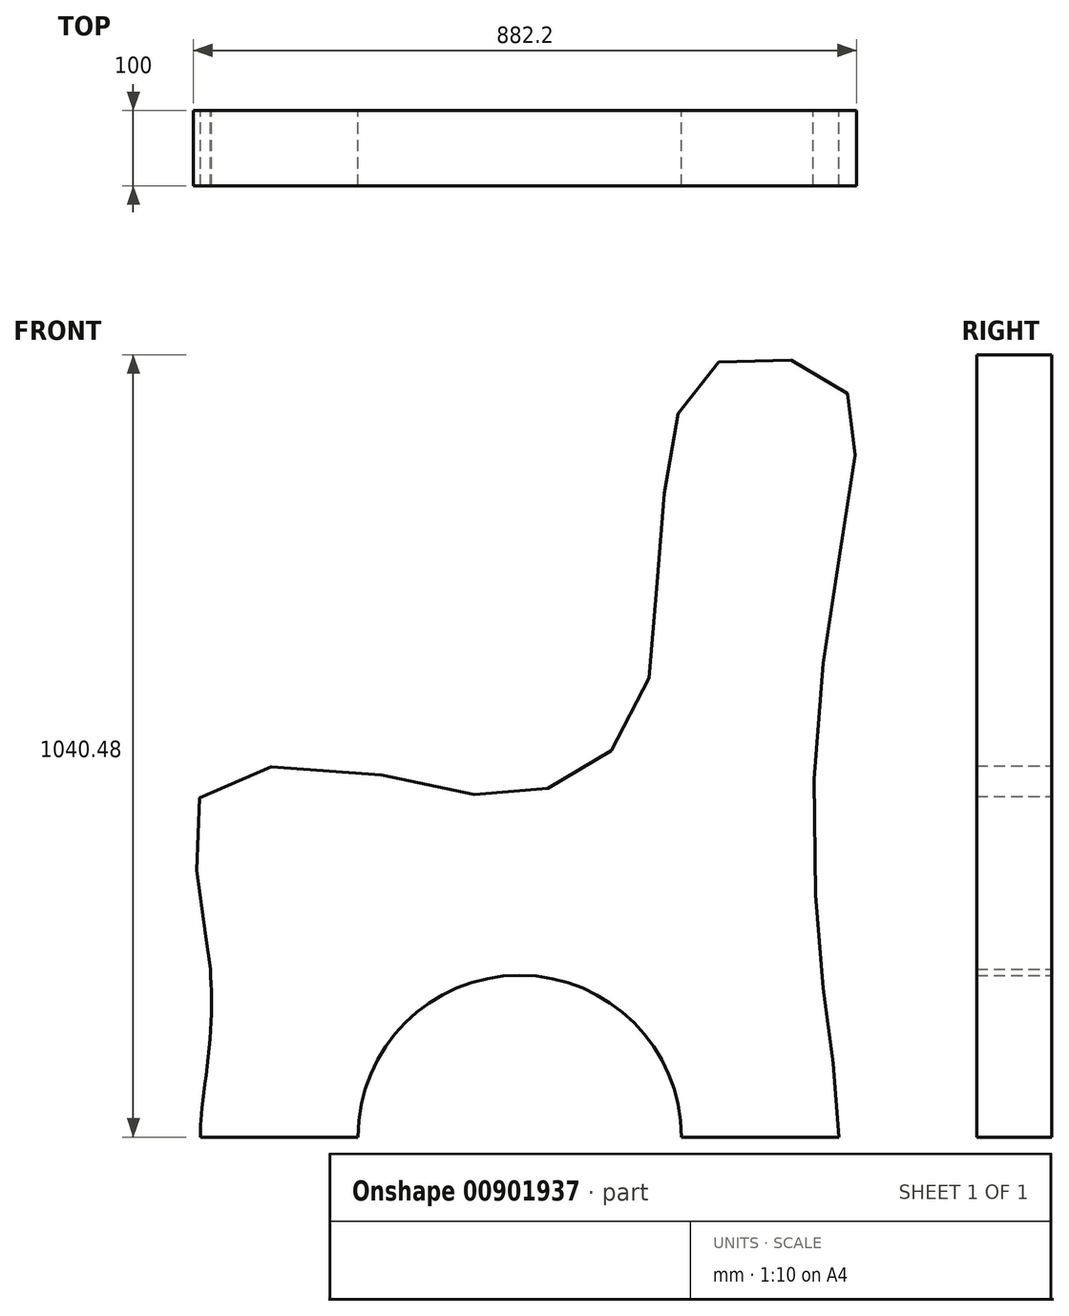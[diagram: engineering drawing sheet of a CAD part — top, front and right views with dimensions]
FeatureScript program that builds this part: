
annotation { "Feature Type Name" : "Feature", "Feature Type Description" : "" }
export const myFeature = defineFeature(function(context is Context, id is Id, definition is map)
    precondition{}
    {
        {
            var Q0;
            Q0=qCreatedBy(makeId("Front.planeOp"),FACE);
            var sketch = newSketch(context, id + "F0", { "sketchPlane" : qUnion([Q0])});
            skLineSegment(sketch, "E0.top", {"start": v(-120.4, 0) * mm, "end": v(89.2, 0) * mm});
            skArc(sketch, "E1", {"start": v(519.54, 0) * mm, "mid": v(304.37, 215.17) * mm, "end": v(89.2, 0) * mm});
            skPoint(sketch, "E2", {"position": v(89.2, 0) * mm});
            skPoint(sketch, "E3", {"position": v(519.54, 0) * mm});
            skPoint(sketch, "E4", {"position": v(2163.05, 999.8) * mm});
            skLineSegment(sketch, "E5.trimOffspring", {"start": v(519.54, 0) * mm, "end": v(729.13, 0) * mm});
            skFitSpline(sketch, "E6", {"points": [v(729.13, 0) * mm, v(719.38, 115.97) * mm, v(703.41, 242.53) * mm, v(696.86, 499.2) * mm, v(729.13, 767.2) * mm, v(752.3, 947.43) * mm, v(729.13, 1001.96) * mm, v(627.83, 1040.2) * mm, v(539.47, 1009.4) * mm, v(503.13, 902.61) * mm, v(487.59, 742.7) * mm, v(462, 563.77) * mm, v(374.63, 477.82) * mm, v(270.05, 453.35) * mm, v(84.05, 487.52) * mm, v(-109.48, 466.77) * mm, v(-127.25, 370.43) * mm, v(-114.23, 270.71) * mm, v(-109.21, 241.13) * mm, v(-107.2, 223.06) * mm, v(-292.36, 433.36) * mm], "startDerivative": vector(94.95, 2100.32) * mm, "endDerivative": vector(-3611.5, 2895.18) * mm});
            skFitSpline(sketch, "E7", {"points": [v(-107.2, 223.06) * mm, v(-107.2, 136.48) * mm, v(-119.24, 31.12) * mm, v(-120.4, 0) * mm], "startDerivative": vector(9.68, -218.42) * mm, "endDerivative": vector(0.91, -116.73) * mm});
            skSolve(sketch);
        }
        {
            var Q0;
            Q0=makeQuery(id+"F0.imprint","IMPRINT",FACE,{"disambiguationData":[TD([[makeQuery(id+"F0.imprint","IMPRINT",EDGE,{"derivedFrom":sQuery(id+"F0.wireOp",EDGE,"E0.bottom")}),-1.0]])]});
            var Q1;
            Q1=makeQuery(id+"F0.imprint","IMPRINT",FACE,{"disambiguationData":[TD([[makeQuery(id+"F0.imprint","IMPRINT",EDGE,{"derivedFrom":sQuery(id+"F0.wireOp",EDGE,"E0.top")}),1.0]])]});
            extrude(context, id + "F1", {"entities" : qUnion([Q0, Q1]), "depth" : 100 * mm, "offsetDistance" : 25 * mm});
        }
    });
